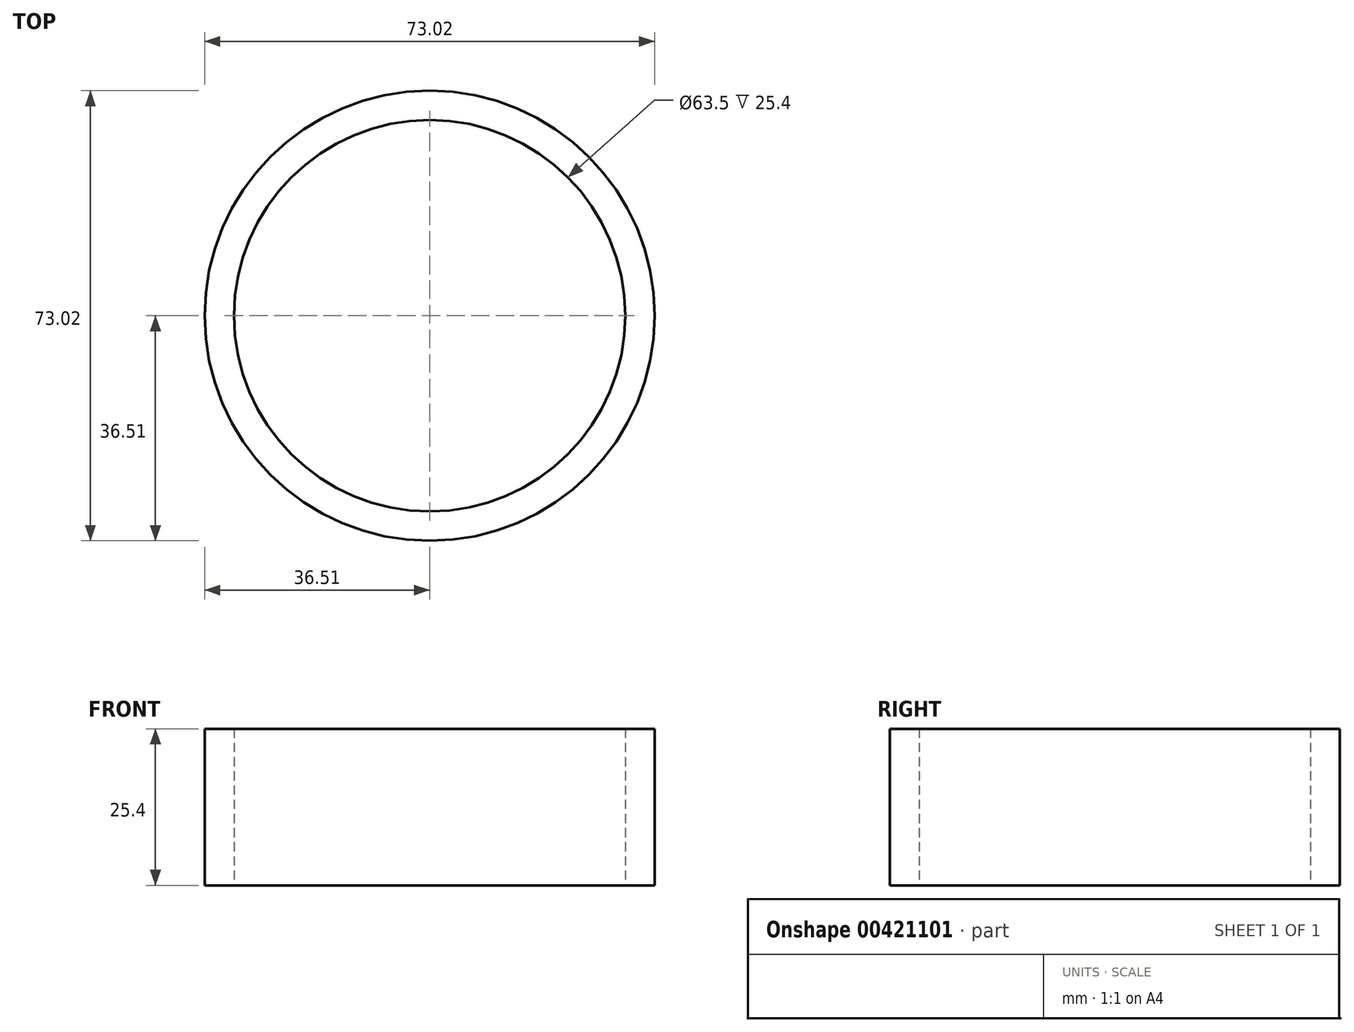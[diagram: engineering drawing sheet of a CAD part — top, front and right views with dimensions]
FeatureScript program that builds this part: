
annotation { "Feature Type Name" : "Feature", "Feature Type Description" : "" }
export const myFeature = defineFeature(function(context is Context, id is Id, definition is map)
    precondition{}
    {
        {
            var Q0;
            Q0=qCreatedBy(makeId("Top.planeOp"),FACE);
            var sketch = newSketch(context, id + "F0", { "sketchPlane" : qUnion([Q0])});
            skCircle(sketch, "E0", {"center": v(0, 0) * mm, "radius": 25.4 * mm});
            skCircle(sketch, "E1", {"center": v(0, 0) * mm, "radius": 30.16 * mm});
            skCircle(sketch, "E2", {"center": v(0, 0) * mm, "radius": 31.75 * mm});
            skCircle(sketch, "E3", {"center": v(0, 0) * mm, "radius": 36.51 * mm});
            skSolve(sketch);
        }
        {
            var Q0;
            Q0 = qSketchRegion(id + "F0", true);
            extrude(context, id + "F1", {"entities" : qUnion([Q0]), "depth" : 25.4 * mm});
        }
    });
